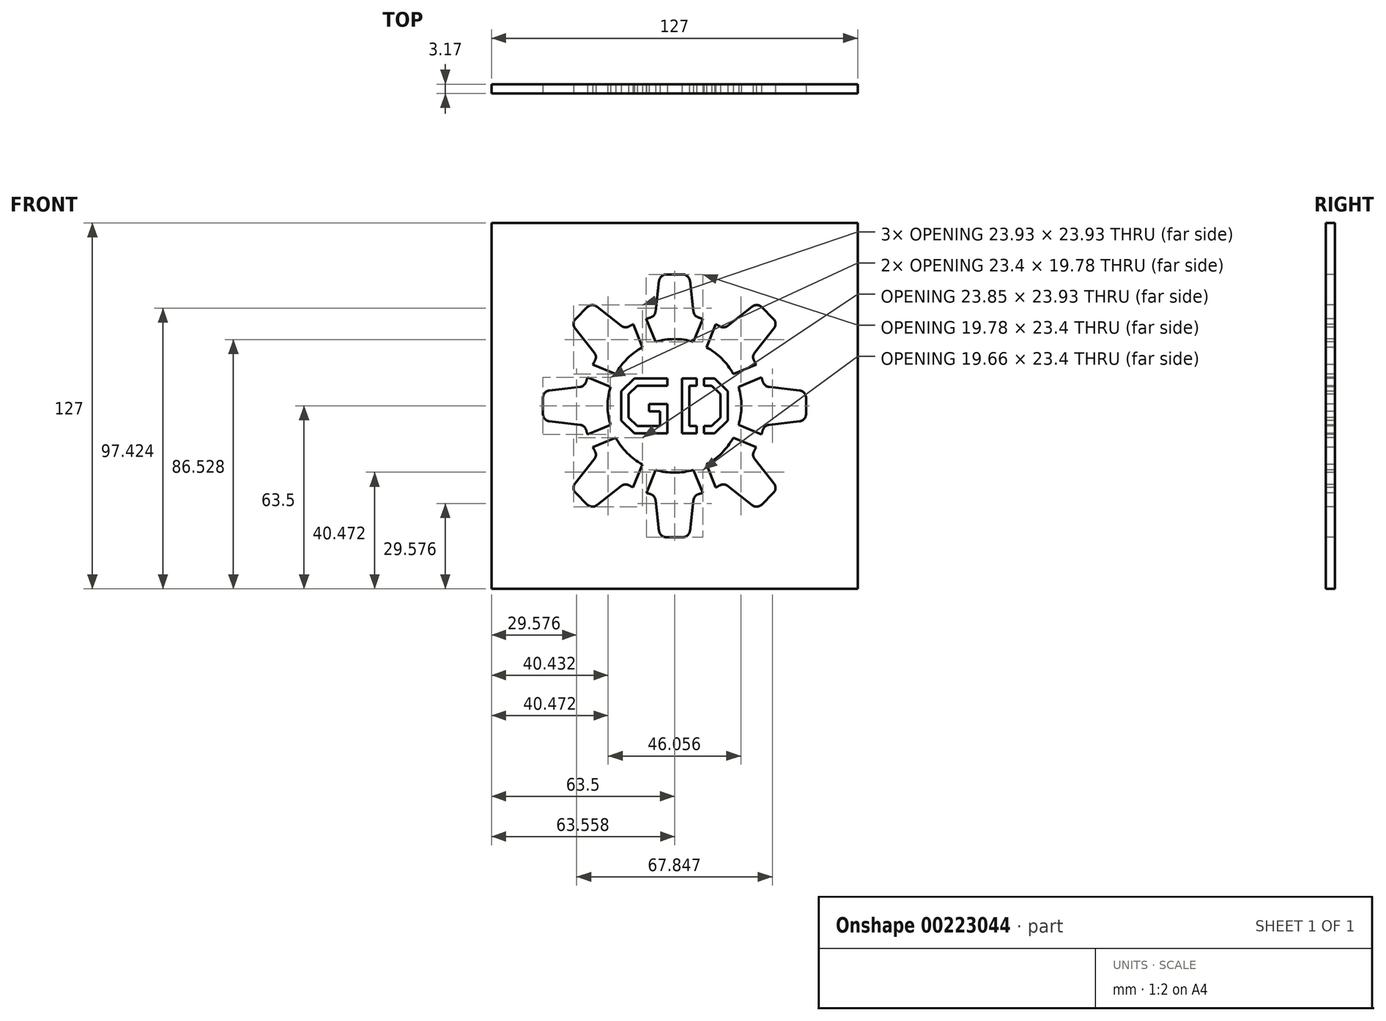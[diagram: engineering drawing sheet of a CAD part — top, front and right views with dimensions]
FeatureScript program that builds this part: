
annotation { "Feature Type Name" : "Feature", "Feature Type Description" : "" }
export const myFeature = defineFeature(function(context is Context, id is Id, definition is map)
    precondition{}
    {
        {
            var Q0;
            Q0=qCreatedBy(makeId("Front.planeOp"),FACE);
            var sketch = newSketch(context, id + "F0", { "sketchPlane" : qUnion([Q0])});
            skLineSegment(sketch, "E0.bottom", {"start": v(63.5, -63.5) * mm, "end": v(-63.5, -63.5) * mm});
            skLineSegment(sketch, "E0.top", {"start": v(63.5, 63.5) * mm, "end": v(-63.5, 63.5) * mm});
            skLineSegment(sketch, "E0.left", {"start": v(63.5, -63.5) * mm, "end": v(63.5, 63.5) * mm});
            skLineSegment(sketch, "E0.right", {"start": v(-63.5, -63.5) * mm, "end": v(-63.5, 63.5) * mm});
            skPoint(sketch, "E0.middle", {"position": v(0, 0) * mm});
            skSolve(sketch);
        }
        {
            var Q0;
            Q0 = qSketchRegion(id + "F0", true);
            extrude(context, id + "F1", {"entities" : qUnion([Q0]), "oppositeDirection" : true, "depth" : 3.17 * mm});
        }
        {
            var Q0;
            Q0=makeQuery(id+"F1.opExtrude","CAP_FACE",FACE,{"disambiguationData":[OSD([sQuery(id+"F0.wireOp",EDGE,"E0.bottom"),sQuery(id+"F0.wireOp",EDGE,"E0.top"),sQuery(id+"F0.wireOp",EDGE,"E0.left"),sQuery(id+"F0.wireOp",EDGE,"E0.right")])],"isStart":true});
            var sketch = newSketch(context, id + "F2", { "sketchPlane" : qUnion([Q0])});
            skArc(sketch, "E1", {"start": v(-8.42, 30.61) * mm, "mid": v(-12.15, 29.33) * mm, "end": v(-15.69, 27.6) * mm});
            skLineSegment(sketch, "E2", {"start": v(0, 0) * mm, "end": v(0, 63.5) * mm});
            skLineSegment(sketch, "E3", {"start": v(-6.58, 32.77) * mm, "end": v(-5.34, 43.38) * mm});
            skLineSegment(sketch, "E4", {"start": v(-2.82, 45.62) * mm, "end": v(0, 45.62) * mm});
            skLineSegment(sketch, "E5.MirrorCS", {"start": v(2.82, 45.62) * mm, "end": v(0, 45.62) * mm});
            skLineSegment(sketch, "E6.MirrorCS", {"start": v(6.58, 32.77) * mm, "end": v(5.34, 43.38) * mm});
            skLineSegment(sketch, "E7.1.0", {"start": v(-27.82, 18.52) * mm, "end": v(-34.45, 26.9) * mm});
            skLineSegment(sketch, "E7.1.1", {"start": v(-34.25, 30.27) * mm, "end": v(-32.26, 32.26) * mm});
            skLineSegment(sketch, "E7.1.2", {"start": v(-30.27, 34.25) * mm, "end": v(-32.26, 32.26) * mm});
            skLineSegment(sketch, "E7.1.3", {"start": v(-18.52, 27.82) * mm, "end": v(-26.9, 34.45) * mm});
            skLineSegment(sketch, "E7.2.0", {"start": v(-32.77, -6.58) * mm, "end": v(-43.38, -5.34) * mm});
            skLineSegment(sketch, "E7.2.1", {"start": v(-45.62, -2.82) * mm, "end": v(-45.62, 0) * mm});
            skLineSegment(sketch, "E7.2.2", {"start": v(-45.62, 2.82) * mm, "end": v(-45.62, 0) * mm});
            skLineSegment(sketch, "E7.2.3", {"start": v(-32.77, 6.58) * mm, "end": v(-43.38, 5.34) * mm});
            skLineSegment(sketch, "E7.3.0", {"start": v(-18.52, -27.82) * mm, "end": v(-26.9, -34.45) * mm});
            skLineSegment(sketch, "E7.3.1", {"start": v(-30.27, -34.25) * mm, "end": v(-32.26, -32.26) * mm});
            skLineSegment(sketch, "E7.3.2", {"start": v(-34.25, -30.27) * mm, "end": v(-32.26, -32.26) * mm});
            skLineSegment(sketch, "E7.3.3", {"start": v(-27.82, -18.52) * mm, "end": v(-34.45, -26.9) * mm});
            skLineSegment(sketch, "E7.4.0", {"start": v(6.58, -32.77) * mm, "end": v(5.34, -43.38) * mm});
            skLineSegment(sketch, "E7.4.1", {"start": v(2.82, -45.62) * mm, "end": v(0, -45.62) * mm});
            skLineSegment(sketch, "E7.4.2", {"start": v(-2.82, -45.62) * mm, "end": v(0, -45.62) * mm});
            skLineSegment(sketch, "E7.4.3", {"start": v(-6.58, -32.77) * mm, "end": v(-5.34, -43.38) * mm});
            skLineSegment(sketch, "E7.5.0", {"start": v(27.82, -18.52) * mm, "end": v(34.45, -26.9) * mm});
            skLineSegment(sketch, "E7.5.1", {"start": v(34.25, -30.27) * mm, "end": v(32.26, -32.26) * mm});
            skLineSegment(sketch, "E7.5.2", {"start": v(30.27, -34.25) * mm, "end": v(32.26, -32.26) * mm});
            skLineSegment(sketch, "E7.5.3", {"start": v(18.52, -27.82) * mm, "end": v(26.9, -34.45) * mm});
            skLineSegment(sketch, "E7.6.0", {"start": v(32.77, 6.58) * mm, "end": v(43.38, 5.34) * mm});
            skLineSegment(sketch, "E7.6.1", {"start": v(45.62, 2.82) * mm, "end": v(45.62, 0) * mm});
            skLineSegment(sketch, "E7.6.2", {"start": v(45.62, -2.82) * mm, "end": v(45.62, 0) * mm});
            skLineSegment(sketch, "E7.6.3", {"start": v(32.77, -6.58) * mm, "end": v(43.38, -5.34) * mm});
            skLineSegment(sketch, "E7.7.0", {"start": v(18.52, 27.82) * mm, "end": v(26.9, 34.45) * mm});
            skLineSegment(sketch, "E7.7.1", {"start": v(30.27, 34.25) * mm, "end": v(32.26, 32.26) * mm});
            skLineSegment(sketch, "E7.7.2", {"start": v(34.25, 30.27) * mm, "end": v(32.26, 32.26) * mm});
            skLineSegment(sketch, "E7.7.3", {"start": v(27.82, 18.52) * mm, "end": v(34.45, 26.9) * mm});
            skArc(sketch, "E8.trimOffspring", {"start": v(15.69, 27.6) * mm, "mid": v(12.15, 29.33) * mm, "end": v(8.42, 30.61) * mm});
            skArc(sketch, "E9.trimOffspring", {"start": v(30.61, 8.42) * mm, "mid": v(29.33, 12.15) * mm, "end": v(27.6, 15.69) * mm});
            skArc(sketch, "E10.trimOffspring", {"start": v(27.6, -15.69) * mm, "mid": v(29.33, -12.15) * mm, "end": v(30.61, -8.42) * mm});
            skArc(sketch, "E11.trimOffspring", {"start": v(8.42, -30.61) * mm, "mid": v(12.15, -29.33) * mm, "end": v(15.69, -27.6) * mm});
            skArc(sketch, "E12.trimOffspring", {"start": v(-15.69, -27.6) * mm, "mid": v(-12.15, -29.33) * mm, "end": v(-8.42, -30.61) * mm});
            skArc(sketch, "E13.trimOffspring", {"start": v(-30.61, -8.42) * mm, "mid": v(-29.33, -12.15) * mm, "end": v(-27.6, -15.69) * mm});
            skArc(sketch, "E14.trimOffspring", {"start": v(-27.6, 15.69) * mm, "mid": v(-29.33, 12.15) * mm, "end": v(-30.61, 8.42) * mm});
            skPoint(sketch, "E15.visualSharp", {"position": v(-17.14, 26.73) * mm});
            skArc(sketch, "E15.filletArc", {"start": v(-18.52, 27.82) * mm, "mid": v(-17.14, 27.28) * mm, "end": v(-15.69, 27.6) * mm});
            skPoint(sketch, "E16.visualSharp", {"position": v(-28.67, 35.85) * mm});
            skArc(sketch, "E16.filletArc", {"start": v(-26.9, 34.45) * mm, "mid": v(-28.62, 35) * mm, "end": v(-30.27, 34.25) * mm});
            skPoint(sketch, "E17.visualSharp", {"position": v(-35.85, 28.67) * mm});
            skArc(sketch, "E17.filletArc", {"start": v(-34.25, 30.27) * mm, "mid": v(-35, 28.62) * mm, "end": v(-34.45, 26.9) * mm});
            skPoint(sketch, "E18.visualSharp", {"position": v(-26.73, 17.14) * mm});
            skArc(sketch, "E18.filletArc", {"start": v(-27.6, 15.69) * mm, "mid": v(-27.28, 17.14) * mm, "end": v(-27.82, 18.52) * mm});
            skPoint(sketch, "E19.visualSharp", {"position": v(-31.02, 6.78) * mm});
            skArc(sketch, "E19.filletArc", {"start": v(-32.77, 6.58) * mm, "mid": v(-31.4, 7.17) * mm, "end": v(-30.61, 8.42) * mm});
            skPoint(sketch, "E20.visualSharp", {"position": v(-45.62, 5.08) * mm});
            skArc(sketch, "E20.filletArc", {"start": v(-43.38, 5.34) * mm, "mid": v(-44.98, 4.5) * mm, "end": v(-45.62, 2.82) * mm});
            skPoint(sketch, "E21.visualSharp", {"position": v(-45.62, -5.08) * mm});
            skArc(sketch, "E21.filletArc", {"start": v(-45.62, -2.82) * mm, "mid": v(-44.98, -4.5) * mm, "end": v(-43.38, -5.34) * mm});
            skPoint(sketch, "E22.visualSharp", {"position": v(-31.02, -6.78) * mm});
            skArc(sketch, "E22.filletArc", {"start": v(-30.61, -8.42) * mm, "mid": v(-31.4, -7.17) * mm, "end": v(-32.77, -6.58) * mm});
            skPoint(sketch, "E23.visualSharp", {"position": v(-26.73, -17.14) * mm});
            skArc(sketch, "E23.filletArc", {"start": v(-27.82, -18.52) * mm, "mid": v(-27.28, -17.14) * mm, "end": v(-27.6, -15.69) * mm});
            skPoint(sketch, "E24.visualSharp", {"position": v(-35.85, -28.67) * mm});
            skArc(sketch, "E24.filletArc", {"start": v(-34.45, -26.9) * mm, "mid": v(-35, -28.62) * mm, "end": v(-34.25, -30.27) * mm});
            skPoint(sketch, "E25.visualSharp", {"position": v(-28.67, -35.85) * mm});
            skArc(sketch, "E25.filletArc", {"start": v(-30.27, -34.25) * mm, "mid": v(-28.62, -35) * mm, "end": v(-26.9, -34.45) * mm});
            skPoint(sketch, "E26.visualSharp", {"position": v(-17.14, -26.73) * mm});
            skArc(sketch, "E26.filletArc", {"start": v(-15.69, -27.6) * mm, "mid": v(-17.14, -27.28) * mm, "end": v(-18.52, -27.82) * mm});
            skPoint(sketch, "E27.visualSharp", {"position": v(-6.78, -31.02) * mm});
            skArc(sketch, "E27.filletArc", {"start": v(-6.58, -32.77) * mm, "mid": v(-7.17, -31.4) * mm, "end": v(-8.42, -30.61) * mm});
            skPoint(sketch, "E28.visualSharp", {"position": v(-5.08, -45.62) * mm});
            skArc(sketch, "E28.filletArc", {"start": v(-5.34, -43.38) * mm, "mid": v(-4.5, -44.98) * mm, "end": v(-2.82, -45.62) * mm});
            skPoint(sketch, "E29.visualSharp", {"position": v(5.08, -45.62) * mm});
            skArc(sketch, "E29.filletArc", {"start": v(2.82, -45.62) * mm, "mid": v(4.5, -44.98) * mm, "end": v(5.34, -43.38) * mm});
            skPoint(sketch, "E30.visualSharp", {"position": v(6.78, -31.02) * mm});
            skArc(sketch, "E30.filletArc", {"start": v(8.42, -30.61) * mm, "mid": v(7.17, -31.4) * mm, "end": v(6.58, -32.77) * mm});
            skPoint(sketch, "E31.visualSharp", {"position": v(17.14, -26.73) * mm});
            skArc(sketch, "E31.filletArc", {"start": v(18.52, -27.82) * mm, "mid": v(17.14, -27.28) * mm, "end": v(15.69, -27.6) * mm});
            skPoint(sketch, "E32.visualSharp", {"position": v(28.67, -35.85) * mm});
            skArc(sketch, "E32.filletArc", {"start": v(26.9, -34.45) * mm, "mid": v(28.62, -35) * mm, "end": v(30.27, -34.25) * mm});
            skPoint(sketch, "E33.visualSharp", {"position": v(35.85, -28.67) * mm});
            skArc(sketch, "E33.filletArc", {"start": v(34.25, -30.27) * mm, "mid": v(35, -28.62) * mm, "end": v(34.45, -26.9) * mm});
            skPoint(sketch, "E34.visualSharp", {"position": v(26.73, -17.14) * mm});
            skArc(sketch, "E34.filletArc", {"start": v(27.6, -15.69) * mm, "mid": v(27.28, -17.14) * mm, "end": v(27.82, -18.52) * mm});
            skPoint(sketch, "E35.visualSharp", {"position": v(31.02, -6.78) * mm});
            skArc(sketch, "E35.filletArc", {"start": v(32.77, -6.58) * mm, "mid": v(31.4, -7.17) * mm, "end": v(30.61, -8.42) * mm});
            skPoint(sketch, "E36.visualSharp", {"position": v(45.62, -5.08) * mm});
            skArc(sketch, "E36.filletArc", {"start": v(43.38, -5.34) * mm, "mid": v(44.98, -4.5) * mm, "end": v(45.62, -2.82) * mm});
            skPoint(sketch, "E37.visualSharp", {"position": v(45.62, 5.08) * mm});
            skArc(sketch, "E37.filletArc", {"start": v(45.62, 2.82) * mm, "mid": v(44.98, 4.5) * mm, "end": v(43.38, 5.34) * mm});
            skPoint(sketch, "E38.visualSharp", {"position": v(31.02, 6.78) * mm});
            skArc(sketch, "E38.filletArc", {"start": v(30.61, 8.42) * mm, "mid": v(31.4, 7.17) * mm, "end": v(32.77, 6.58) * mm});
            skPoint(sketch, "E39.visualSharp", {"position": v(26.73, 17.14) * mm});
            skArc(sketch, "E39.filletArc", {"start": v(27.82, 18.52) * mm, "mid": v(27.28, 17.14) * mm, "end": v(27.6, 15.69) * mm});
            skPoint(sketch, "E40.visualSharp", {"position": v(35.85, 28.67) * mm});
            skArc(sketch, "E40.filletArc", {"start": v(34.45, 26.9) * mm, "mid": v(35, 28.62) * mm, "end": v(34.25, 30.27) * mm});
            skPoint(sketch, "E41.visualSharp", {"position": v(28.67, 35.85) * mm});
            skArc(sketch, "E41.filletArc", {"start": v(30.27, 34.25) * mm, "mid": v(28.62, 35) * mm, "end": v(26.9, 34.45) * mm});
            skPoint(sketch, "E42.visualSharp", {"position": v(17.14, 26.73) * mm});
            skArc(sketch, "E42.filletArc", {"start": v(15.69, 27.6) * mm, "mid": v(17.14, 27.28) * mm, "end": v(18.52, 27.82) * mm});
            skPoint(sketch, "E43.visualSharp", {"position": v(6.78, 31.02) * mm});
            skArc(sketch, "E43.filletArc", {"start": v(6.58, 32.77) * mm, "mid": v(7.17, 31.4) * mm, "end": v(8.42, 30.61) * mm});
            skPoint(sketch, "E44.visualSharp", {"position": v(-5.08, 45.62) * mm});
            skArc(sketch, "E44.filletArc", {"start": v(-2.82, 45.62) * mm, "mid": v(-4.5, 44.98) * mm, "end": v(-5.34, 43.38) * mm});
            skPoint(sketch, "E45.visualSharp", {"position": v(-6.78, 31.02) * mm});
            skArc(sketch, "E45.filletArc", {"start": v(-8.42, 30.61) * mm, "mid": v(-7.17, 31.4) * mm, "end": v(-6.58, 32.77) * mm});
            skArc(sketch, "E46.MirrorCS", {"start": v(2.82, 45.62) * mm, "mid": v(4.5, 44.98) * mm, "end": v(5.34, 43.38) * mm});
            skPoint(sketch, "E47.MirrorCS.end.orphan", {"position": v(0, 45.62) * mm});
            skPoint(sketch, "E48.orphan", {"position": v(5.08, 45.62) * mm});
            skCircle(sketch, "E49", {"center": v(0, 0) * mm, "radius": 23.18 * mm});
            skLineSegment(sketch, "E50", {"start": v(14.34, 28.33) * mm, "end": v(11.06, 20.37) * mm});
            skLineSegment(sketch, "E51", {"start": v(12.15, 29.33) * mm, "end": v(-12.15, -29.33) * mm});
            skLineSegment(sketch, "E52.MirrorCS", {"start": v(9.89, 30.17) * mm, "end": v(6.58, 22.22) * mm});
            skLineSegment(sketch, "E53.trimOffspring", {"start": v(-6.5, -22.25) * mm, "end": v(-9.77, -30.2) * mm});
            skLineSegment(sketch, "E54.trimOffspring", {"start": v(-11.14, -20.32) * mm, "end": v(-14.45, -28.27) * mm});
            skSolve(sketch);
        }
        {
            var Q0;
            Q0 = qSketchRegion(id + "F2", true);
            var Q1;
            Q1=makeQuery(id+"F1.opExtrude","CAP_FACE",FACE,{"disambiguationData":[OSD([sQuery(id+"F0.wireOp",EDGE,"E0.bottom"),sQuery(id+"F0.wireOp",EDGE,"E0.top"),sQuery(id+"F0.wireOp",EDGE,"E0.left"),sQuery(id+"F0.wireOp",EDGE,"E0.right")])],"isStart":false});
            extrude(context, id + "F3", {"entities" : qUnion([Q0]), "operationType" : NewBodyOperationType.REMOVE, "endBound" : BoundingType.UP_TO_SURFACE, "oppositeDirection" : true, "endBoundEntityFace" : qUnion([Q1]), "depth" : 25.4 * mm});
        }
        {
            var Q0;
            {var subQ0=sQuery(id+"F0.wireOp",EDGE,"E0.top");var subQ1=sQuery(id+"F0.wireOp",EDGE,"E0.right");var subQ2=sQuery(id+"F0.wireOp",EDGE,"E0.bottom");var subQ3=sQuery(id+"F0.wireOp",EDGE,"E0.left");Q0=makeQuery(id+"F3.boolean.opBoolean","SPLIT",FACE,{"disambiguationData":[TD([makeQuery(id+"F1.opExtrude","SWEPT_FACE",FACE,{"disambiguationData":[OSD([subQ2])]})])],"derivedFrom":makeQuery(id+"F1.opExtrude","CAP_FACE",FACE,{"disambiguationData":[OSD([subQ2,subQ0,subQ3,subQ1])],"isStart":true})});}
            var sketch = newSketch(context, id + "F4", { "sketchPlane" : qUnion([Q0])});
            skLineSegment(sketch, "E55", {"start": v(14.34, 28.33) * mm, "end": v(11.06, 20.37) * mm});
            skLineSegment(sketch, "E56", {"start": v(9.89, 30.17) * mm, "end": v(6.58, 22.22) * mm});
            skLineSegment(sketch, "E57", {"start": v(-6.5, -22.25) * mm, "end": v(-9.77, -30.2) * mm});
            skLineSegment(sketch, "E58", {"start": v(-11.14, -20.32) * mm, "end": v(-14.45, -28.27) * mm});
            skLineSegment(sketch, "E59", {"start": v(6.58, 22.22) * mm, "end": v(6.58, 19.24) * mm});
            skLineSegment(sketch, "E60", {"start": v(6.58, 19.24) * mm, "end": v(11.06, 20.37) * mm});
            skLineSegment(sketch, "E61", {"start": v(-6.5, -22.25) * mm, "end": v(-7.96, -16.93) * mm});
            skLineSegment(sketch, "E62", {"start": v(-7.96, -16.93) * mm, "end": v(-11.14, -20.32) * mm});
            skLineSegment(sketch, "E63", {"start": v(-14.45, -28.27) * mm, "end": v(-13.84, -33.36) * mm});
            skLineSegment(sketch, "E64", {"start": v(-13.84, -33.36) * mm, "end": v(-9.77, -30.2) * mm});
            skLineSegment(sketch, "E65", {"start": v(9.89, 30.17) * mm, "end": v(14.34, 32.37) * mm});
            skLineSegment(sketch, "E66", {"start": v(14.34, 32.37) * mm, "end": v(14.34, 28.33) * mm});
            skLineSegment(sketch, "E67.1.0", {"start": v(-14.34, 28.33) * mm, "end": v(-12.75, 33.03) * mm});
            skLineSegment(sketch, "E67.1.1", {"start": v(-9.89, 30.17) * mm, "end": v(-6.58, 22.22) * mm});
            skLineSegment(sketch, "E67.1.2", {"start": v(-14.34, 28.33) * mm, "end": v(-11.06, 20.37) * mm});
            skLineSegment(sketch, "E67.1.3", {"start": v(-8.95, 18.25) * mm, "end": v(-6.58, 22.22) * mm});
            skLineSegment(sketch, "E67.1.4", {"start": v(-11.06, 20.37) * mm, "end": v(-8.95, 18.25) * mm});
            skLineSegment(sketch, "E67.1.5", {"start": v(-12.75, 33.03) * mm, "end": v(-9.89, 30.17) * mm});
            skLineSegment(sketch, "E67.2.0", {"start": v(-30.17, 9.89) * mm, "end": v(-32.37, 14.34) * mm});
            skLineSegment(sketch, "E67.2.1", {"start": v(-28.33, 14.34) * mm, "end": v(-20.37, 11.06) * mm});
            skLineSegment(sketch, "E67.2.2", {"start": v(-30.17, 9.89) * mm, "end": v(-22.22, 6.58) * mm});
            skLineSegment(sketch, "E67.2.3", {"start": v(-19.24, 6.58) * mm, "end": v(-20.37, 11.06) * mm});
            skLineSegment(sketch, "E67.2.4", {"start": v(-22.22, 6.58) * mm, "end": v(-19.24, 6.58) * mm});
            skLineSegment(sketch, "E67.2.5", {"start": v(-32.37, 14.34) * mm, "end": v(-28.33, 14.34) * mm});
            skLineSegment(sketch, "E67.3.0", {"start": v(-28.33, -14.34) * mm, "end": v(-33.03, -12.75) * mm});
            skLineSegment(sketch, "E67.3.1", {"start": v(-30.17, -9.89) * mm, "end": v(-22.22, -6.58) * mm});
            skLineSegment(sketch, "E67.3.2", {"start": v(-28.33, -14.34) * mm, "end": v(-20.37, -11.06) * mm});
            skLineSegment(sketch, "E67.3.3", {"start": v(-18.25, -8.95) * mm, "end": v(-22.22, -6.58) * mm});
            skLineSegment(sketch, "E67.3.4", {"start": v(-20.37, -11.06) * mm, "end": v(-18.25, -8.95) * mm});
            skLineSegment(sketch, "E67.3.5", {"start": v(-33.03, -12.75) * mm, "end": v(-30.17, -9.89) * mm});
            skLineSegment(sketch, "E67.4.0", {"start": v(-9.89, -30.17) * mm, "end": v(-14.34, -32.37) * mm});
            skLineSegment(sketch, "E67.4.1", {"start": v(-14.34, -28.33) * mm, "end": v(-11.06, -20.37) * mm});
            skLineSegment(sketch, "E67.4.2", {"start": v(-9.89, -30.17) * mm, "end": v(-6.58, -22.22) * mm});
            skLineSegment(sketch, "E67.4.3", {"start": v(-6.58, -19.24) * mm, "end": v(-11.06, -20.37) * mm});
            skLineSegment(sketch, "E67.4.4", {"start": v(-6.58, -22.22) * mm, "end": v(-6.58, -19.24) * mm});
            skLineSegment(sketch, "E67.4.5", {"start": v(-14.34, -32.37) * mm, "end": v(-14.34, -28.33) * mm});
            skLineSegment(sketch, "E67.5.0", {"start": v(14.34, -28.33) * mm, "end": v(12.75, -33.03) * mm});
            skLineSegment(sketch, "E67.5.1", {"start": v(9.89, -30.17) * mm, "end": v(6.58, -22.22) * mm});
            skLineSegment(sketch, "E67.5.2", {"start": v(14.34, -28.33) * mm, "end": v(11.06, -20.37) * mm});
            skLineSegment(sketch, "E67.5.3", {"start": v(8.95, -18.25) * mm, "end": v(6.58, -22.22) * mm});
            skLineSegment(sketch, "E67.5.4", {"start": v(11.06, -20.37) * mm, "end": v(8.95, -18.25) * mm});
            skLineSegment(sketch, "E67.5.5", {"start": v(12.75, -33.03) * mm, "end": v(9.89, -30.17) * mm});
            skLineSegment(sketch, "E67.6.0", {"start": v(30.17, -9.89) * mm, "end": v(32.37, -14.34) * mm});
            skLineSegment(sketch, "E67.6.1", {"start": v(28.33, -14.34) * mm, "end": v(20.37, -11.06) * mm});
            skLineSegment(sketch, "E67.6.2", {"start": v(30.17, -9.89) * mm, "end": v(22.22, -6.58) * mm});
            skLineSegment(sketch, "E67.6.3", {"start": v(19.24, -6.58) * mm, "end": v(20.37, -11.06) * mm});
            skLineSegment(sketch, "E67.6.4", {"start": v(22.22, -6.58) * mm, "end": v(19.24, -6.58) * mm});
            skLineSegment(sketch, "E67.6.5", {"start": v(32.37, -14.34) * mm, "end": v(28.33, -14.34) * mm});
            skLineSegment(sketch, "E67.7.0", {"start": v(28.33, 14.34) * mm, "end": v(33.03, 12.75) * mm});
            skLineSegment(sketch, "E67.7.1", {"start": v(30.17, 9.89) * mm, "end": v(22.22, 6.58) * mm});
            skLineSegment(sketch, "E67.7.2", {"start": v(28.33, 14.34) * mm, "end": v(20.37, 11.06) * mm});
            skLineSegment(sketch, "E67.7.3", {"start": v(18.25, 8.95) * mm, "end": v(22.22, 6.58) * mm});
            skLineSegment(sketch, "E67.7.4", {"start": v(20.37, 11.06) * mm, "end": v(18.25, 8.95) * mm});
            skLineSegment(sketch, "E67.7.5", {"start": v(33.03, 12.75) * mm, "end": v(30.17, 9.89) * mm});
            skPoint(sketch, "E67.center", {"position": v(0, 0) * mm});
            skSolve(sketch);
        }
        {
            var Q0;
            Q0 = qSketchRegion(id + "F4", true);
            var Q1;
            {var subQ0=sQuery(id+"F0.wireOp",EDGE,"E0.top");var subQ1=sQuery(id+"F0.wireOp",EDGE,"E0.right");var subQ2=sQuery(id+"F0.wireOp",EDGE,"E0.bottom");var subQ3=sQuery(id+"F0.wireOp",EDGE,"E0.left");Q1=makeQuery(id+"F3.boolean.opBoolean","SPLIT",FACE,{"disambiguationData":[TD([makeQuery(id+"F1.opExtrude","SWEPT_FACE",FACE,{"disambiguationData":[OSD([subQ2])]})])],"derivedFrom":makeQuery(id+"F1.opExtrude","CAP_FACE",FACE,{"disambiguationData":[OSD([subQ2,subQ0,subQ3,subQ1])],"isStart":false})});}
            extrude(context, id + "F5", {"entities" : qUnion([Q0]), "operationType" : NewBodyOperationType.ADD, "endBound" : BoundingType.UP_TO_SURFACE, "oppositeDirection" : true, "endBoundEntityFace" : qUnion([Q1]), "depth" : 25.4 * mm});
        }
        {
            var Q0;
            {var subQ0=sQuery(id+"F0.wireOp",EDGE,"E0.right");var subQ1=sQuery(id+"F0.wireOp",EDGE,"E0.left");var subQ2=sQuery(id+"F0.wireOp",EDGE,"E0.top");var subQ3=sQuery(id+"F0.wireOp",EDGE,"E0.bottom");var subQ4=makeQuery(id+"F1.opExtrude","CAP_FACE",FACE,{"disambiguationData":[OSD([subQ3,subQ2,subQ1,subQ0])],"isStart":true});Q0=makeQuery(id+"F5.boolean.opBoolean","MERGE",FACE,{"derivedFrom":[makeQuery(id+"F3.boolean.opBoolean","SPLIT",FACE,{"disambiguationData":[TD([makeQuery(id+"F1.opExtrude","SWEPT_FACE",FACE,{"disambiguationData":[OSD([subQ3])]})])],"derivedFrom":subQ4}),makeQuery(id+"F3.boolean.opBoolean","SPLIT",FACE,{"disambiguationData":[TD([makeQuery(id+"F3.opExtrude","SWEPT_FACE",FACE,{"disambiguationData":[OSD([sQuery(id+"F2.wireOp",EDGE,"E49")])]})])],"derivedFrom":subQ4}),makeQuery(id+"F5.opExtrude","CAP_FACE",FACE,{"disambiguationData":[OSD([sQuery(id+"F4.wireOp",EDGE,"E55"),sQuery(id+"F4.wireOp",EDGE,"E56"),sQuery(id+"F4.wireOp",EDGE,"E59"),sQuery(id+"F4.wireOp",EDGE,"E60"),sQuery(id+"F4.wireOp",EDGE,"E65"),sQuery(id+"F4.wireOp",EDGE,"E66")])],"isStart":true}),makeQuery(id+"F5.opExtrude","CAP_FACE",FACE,{"disambiguationData":[OSD([sQuery(id+"F4.wireOp",EDGE,"E57"),sQuery(id+"F4.wireOp",EDGE,"E58"),sQuery(id+"F4.wireOp",EDGE,"E61"),sQuery(id+"F4.wireOp",EDGE,"E62"),sQuery(id+"F4.wireOp",EDGE,"E63"),sQuery(id+"F4.wireOp",EDGE,"E64")])],"isStart":true})]});}
            var sketch = newSketch(context, id + "F6", { "sketchPlane" : qUnion([Q0])});
            skLineSegment(sketch, "E68", {"start": v(-2.54, 9.57) * mm, "end": v(-13.97, 9.57) * mm});
            skLineSegment(sketch, "E69", {"start": v(-13.97, 9.57) * mm, "end": v(-18.46, 5.08) * mm});
            skLineSegment(sketch, "E70", {"start": v(-18.46, 5.08) * mm, "end": v(-18.46, -5.08) * mm});
            skLineSegment(sketch, "E71", {"start": v(-18.46, -5.08) * mm, "end": v(-13.97, -9.57) * mm});
            skLineSegment(sketch, "E72", {"start": v(-13.97, -9.57) * mm, "end": v(-2.54, -9.57) * mm});
            skLineSegment(sketch, "E73", {"start": v(-2.54, -9.57) * mm, "end": v(-2.54, -7.03) * mm});
            skLineSegment(sketch, "E74", {"start": v(-5.08, -7.03) * mm, "end": v(-12.92, -7.03) * mm});
            skLineSegment(sketch, "E75", {"start": v(-12.92, -7.03) * mm, "end": v(-15.92, -4.03) * mm});
            skLineSegment(sketch, "E76", {"start": v(-15.92, -4.03) * mm, "end": v(-15.92, 4.03) * mm});
            skLineSegment(sketch, "E77", {"start": v(-15.92, 4.03) * mm, "end": v(-12.92, 7.03) * mm});
            skLineSegment(sketch, "E78", {"start": v(-12.92, 7.03) * mm, "end": v(-2.54, 7.03) * mm});
            skLineSegment(sketch, "E79", {"start": v(-2.54, 7.03) * mm, "end": v(-2.54, 9.57) * mm});
            skLineSegment(sketch, "E80", {"start": v(-2.54, -7.03) * mm, "end": v(-2.54, 0.59) * mm});
            skPoint(sketch, "E80.endSnap0", {"position": v(-2.54, -8.3) * mm});
            skLineSegment(sketch, "E81", {"start": v(-2.54, 0.59) * mm, "end": v(-8.9, 0.59) * mm});
            skLineSegment(sketch, "E82", {"start": v(-8.9, 0.59) * mm, "end": v(-8.9, -1.95) * mm});
            skLineSegment(sketch, "E83", {"start": v(-8.9, -1.95) * mm, "end": v(-5.08, -1.95) * mm});
            skLineSegment(sketch, "E84", {"start": v(-5.08, -1.95) * mm, "end": v(-5.08, -7.03) * mm});
            skLineSegment(sketch, "E85", {"start": v(-7.73, 7.03) * mm, "end": v(-7.73, -9.18) * mm, "construction": true});
            skLineSegment(sketch, "E86", {"start": v(-15.92, 0) * mm, "end": v(0, 0) * mm, "construction": true});
            skPoint(sketch, "E87", {"position": v(-7.73, 0) * mm});
            skLineSegment(sketch, "E88", {"start": v(2.54, 9.57) * mm, "end": v(2.54, -9.57) * mm});
            skLineSegment(sketch, "E89", {"start": v(2.54, -9.57) * mm, "end": v(7.72, -9.57) * mm});
            skLineSegment(sketch, "E90", {"start": v(13.95, -9.57) * mm, "end": v(18.47, -5.11) * mm});
            skLineSegment(sketch, "E91", {"start": v(2.54, 0) * mm, "end": v(10.47, 0) * mm, "construction": true});
            skLineSegment(sketch, "E92", {"start": v(18.47, -5.11) * mm, "end": v(18.47, 0) * mm});
            skLineSegment(sketch, "E93.MirrorCS", {"start": v(2.54, 9.57) * mm, "end": v(7.72, 9.57) * mm});
            skLineSegment(sketch, "E94.MirrorCS", {"start": v(13.95, 9.57) * mm, "end": v(18.47, 5.11) * mm});
            skLineSegment(sketch, "E95.MirrorCS", {"start": v(18.47, 5.11) * mm, "end": v(18.47, 0) * mm});
            skLineSegment(sketch, "E96.0", {"start": v(5.08, 7.03) * mm, "end": v(5.08, -7.03) * mm});
            skLineSegment(sketch, "E96.1", {"start": v(5.08, -7.03) * mm, "end": v(7.72, -7.03) * mm});
            skLineSegment(sketch, "E96.2", {"start": v(12.9, 7.03) * mm, "end": v(15.93, 4.05) * mm});
            skLineSegment(sketch, "E96.3", {"start": v(15.93, 4.05) * mm, "end": v(15.93, 0) * mm});
            skLineSegment(sketch, "E96.4", {"start": v(15.93, -4.05) * mm, "end": v(15.93, 0) * mm});
            skLineSegment(sketch, "E96.5", {"start": v(5.08, 7.03) * mm, "end": v(7.72, 7.03) * mm});
            skLineSegment(sketch, "E96.6", {"start": v(12.9, -7.03) * mm, "end": v(15.93, -4.05) * mm});
            skLineSegment(sketch, "E97", {"start": v(0, 0) * mm, "end": v(2.54, 0) * mm, "construction": true});
            skLineSegment(sketch, "E98", {"start": v(9, 7.03) * mm, "end": v(9, 11.23) * mm, "construction": true});
            skLineSegment(sketch, "E99", {"start": v(7.72, 7.03) * mm, "end": v(7.72, 9.57) * mm});
            skLineSegment(sketch, "E100.MirrorCS", {"start": v(10.26, 7.03) * mm, "end": v(10.26, 9.57) * mm});
            skLineSegment(sketch, "E101.trimOffspring", {"start": v(10.26, 9.57) * mm, "end": v(13.95, 9.57) * mm});
            skLineSegment(sketch, "E102.trimOffspring", {"start": v(10.26, 7.03) * mm, "end": v(12.9, 7.03) * mm});
            skLineSegment(sketch, "E103.MirrorCS", {"start": v(10.26, -7.03) * mm, "end": v(10.26, -9.57) * mm});
            skLineSegment(sketch, "E104.MirrorCS", {"start": v(7.72, -7.03) * mm, "end": v(7.72, -9.57) * mm});
            skLineSegment(sketch, "E105.trimOffspring", {"start": v(10.26, -7.03) * mm, "end": v(12.9, -7.03) * mm});
            skLineSegment(sketch, "E106.trimOffspring", {"start": v(10.26, -9.57) * mm, "end": v(13.95, -9.57) * mm});
            skSolve(sketch);
        }
        {
            var Q0;
            Q0 = qSketchRegion(id + "F6", true);
            var Q1;
            {var subQ0=sQuery(id+"F0.wireOp",EDGE,"E0.right");var subQ1=sQuery(id+"F0.wireOp",EDGE,"E0.left");var subQ2=sQuery(id+"F0.wireOp",EDGE,"E0.top");var subQ3=sQuery(id+"F0.wireOp",EDGE,"E0.bottom");var subQ4=makeQuery(id+"F1.opExtrude","CAP_FACE",FACE,{"disambiguationData":[OSD([subQ3,subQ2,subQ1,subQ0])],"isStart":false});Q1=makeQuery(id+"F5.boolean.opBoolean","MERGE",FACE,{"derivedFrom":[makeQuery(id+"F3.boolean.opBoolean","SPLIT",FACE,{"disambiguationData":[TD([makeQuery(id+"F1.opExtrude","SWEPT_FACE",FACE,{"disambiguationData":[OSD([subQ3])]})])],"derivedFrom":subQ4}),makeQuery(id+"F3.boolean.opBoolean","SPLIT",FACE,{"disambiguationData":[TD([makeQuery(id+"F3.opExtrude","SWEPT_FACE",FACE,{"disambiguationData":[OSD([sQuery(id+"F2.wireOp",EDGE,"E49")])]})])],"derivedFrom":subQ4}),makeQuery(id+"F5.opExtrude","CAP_FACE",FACE,{"disambiguationData":[OSD([subQ3,subQ2,subQ1,subQ0]),ownerDisambiguation([makeQuery(id+"F5.opExtrude","SWEPT_BODY",BODY,{"disambiguationData":[OSD([sQuery(id+"F4.wireOp",EDGE,"E55"),sQuery(id+"F4.wireOp",EDGE,"E56"),sQuery(id+"F4.wireOp",EDGE,"E59"),sQuery(id+"F4.wireOp",EDGE,"E60"),sQuery(id+"F4.wireOp",EDGE,"E65"),sQuery(id+"F4.wireOp",EDGE,"E66")])]})])],"isStart":false}),makeQuery(id+"F5.opExtrude","CAP_FACE",FACE,{"disambiguationData":[OSD([subQ3,subQ2,subQ1,subQ0]),ownerDisambiguation([makeQuery(id+"F5.opExtrude","SWEPT_BODY",BODY,{"disambiguationData":[OSD([sQuery(id+"F4.wireOp",EDGE,"E57"),sQuery(id+"F4.wireOp",EDGE,"E58"),sQuery(id+"F4.wireOp",EDGE,"E61"),sQuery(id+"F4.wireOp",EDGE,"E62"),sQuery(id+"F4.wireOp",EDGE,"E63"),sQuery(id+"F4.wireOp",EDGE,"E64")])]})])],"isStart":false})]});}
            extrude(context, id + "F7", {"entities" : qUnion([Q0]), "operationType" : NewBodyOperationType.REMOVE, "endBound" : BoundingType.UP_TO_SURFACE, "oppositeDirection" : true, "endBoundEntityFace" : qUnion([Q1]), "depth" : 25.4 * mm});
        }
    });
